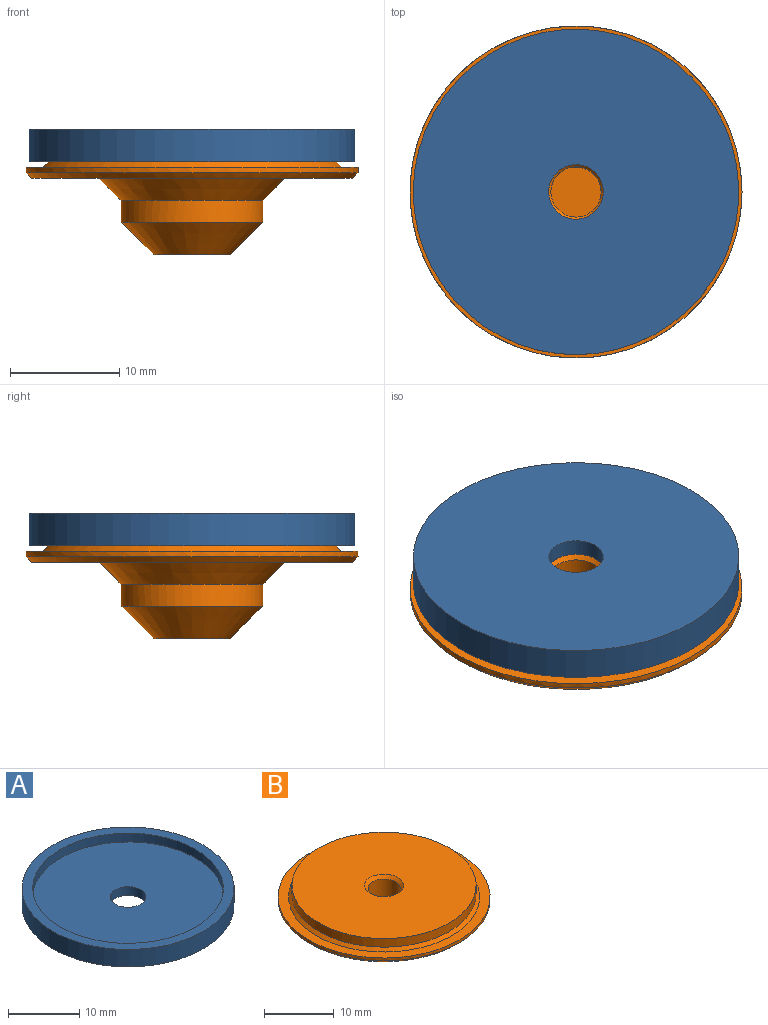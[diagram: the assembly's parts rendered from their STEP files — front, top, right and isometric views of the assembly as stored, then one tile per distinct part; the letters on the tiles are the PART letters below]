
ASSEMBLY  parts=2 mates=1
PART A: 6 faces, bbox 29.8x29.8x3 mm
  f0: cylinder r=2.5mm len=5mm, axis (0,0,1), area 23.6mm2, adj f2,f5
  f1: cylinder r=14.9mm len=29.8mm, axis (0,0,1), area 280.9mm2, adj f2,f3
  f2: plane 29.8x29.8mm, normal (0,0,-1), area 677.8mm2, adj f0,f1
  f3: plane 29.8x29.8mm, normal (0,0,1), area 133.4mm2, adj f1,f4
  f4: cylinder r=13.4mm len=26.8mm, axis (0,0,1), area 126.3mm2, adj f3,f5
  f5: plane 26.8x26.8mm, normal (0,0,1), area 544.5mm2, adj f0,f4
PART B: 14 faces, bbox 30.4x30.4x10 mm
  f0: cylinder r=15.2mm len=30.4mm, axis (0,0,1), area 47.8mm2, adj f2,f12
  f1: cylinder r=13.2mm len=26.4mm, axis (0,0,1), area 124.4mm2, adj f3,f11
  f2: plane 30.4x30.4mm, normal (0,0,1), area 136.2mm2, adj f0,f11
  f3: plane 26.4x26.4mm, normal (0,0,1), area 522.8mm2, adj f1,f10
  f4: cylinder r=6.5mm len=13mm, axis (0,0,-1), area 81.7mm2, adj f9,f13
  f5: plane 29.4x29.4mm, normal (0,0,-1), area 451.9mm2, adj f12,f13
  f6: plane 7x7mm, normal (0,0,-1), area 38.5mm2, adj f9
  f7: cylinder r=2.3mm len=8mm, axis (0,0,1), area 115.6mm2, adj f8,f10
  f8: plane 4.6x4.6mm, normal (0,0,1), area 16.6mm2, adj f7
  f9: cone r=3.5mm half-angle=45deg, axis (0,0,1), area 133.3mm2, adj f4,f6
  f10: cone r=2.3mm half-angle=45deg, axis (0,0,1), area 11.3mm2, adj f3,f7
  f11: cone r=13.2mm half-angle=45deg, axis (0,0,-1), area 59.8mm2, adj f1,f2
  f12: cone r=15.2mm half-angle=45deg, axis (0,0,1), area 66.4mm2, adj f0,f5
  f13: cone r=6.5mm half-angle=45deg, axis (0,0,1), area 133.3mm2, adj f4,f5
PLACE A rot(axis=(0.94,-0.34,0),180deg) t=(-4.94,-3.22,0.14)mm
PLACE B t=(-4.94,-3.22,1.64)mm fixed
MATE cylindrical A.f4 <-> B.f7  axis (0,0,-1) through (-4.94,-3.22,1.64)mm
